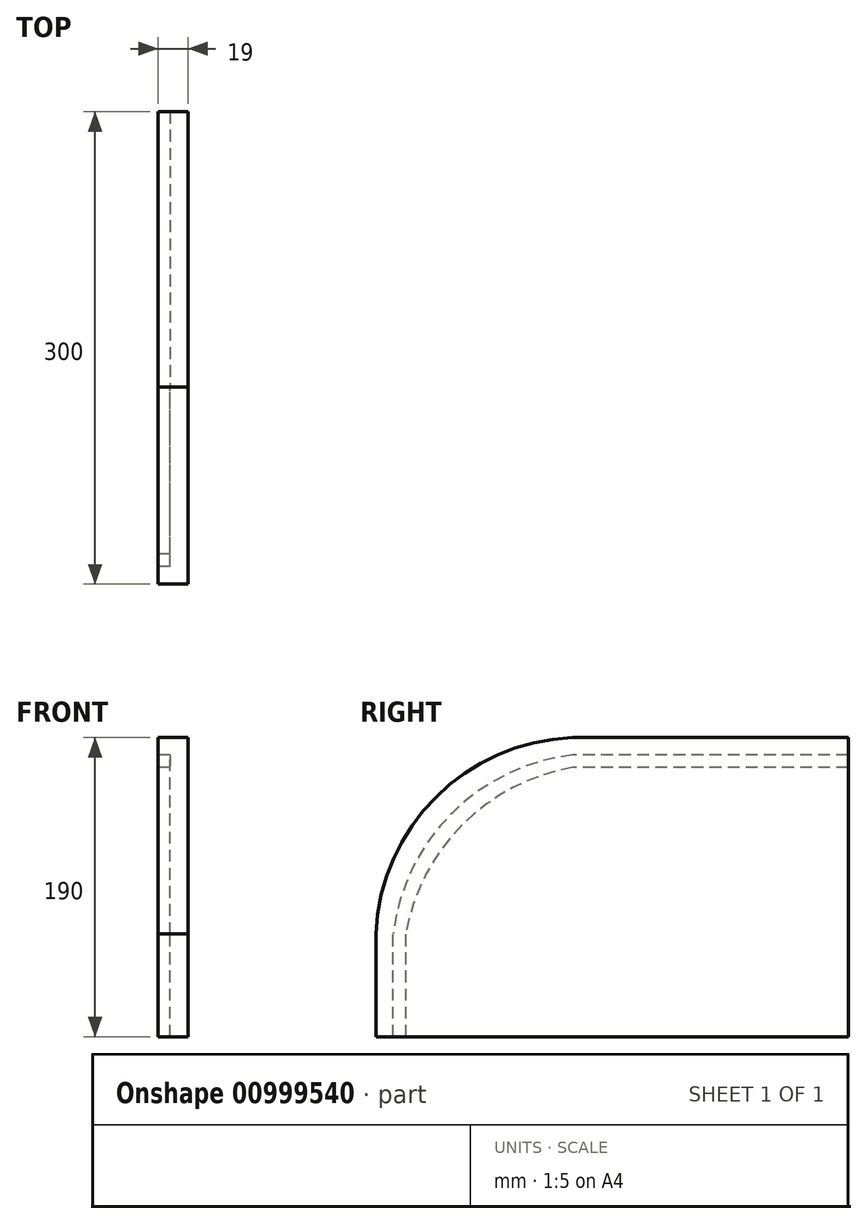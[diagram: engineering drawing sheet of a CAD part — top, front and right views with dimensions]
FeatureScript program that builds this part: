
annotation { "Feature Type Name" : "Feature", "Feature Type Description" : "" }
export const myFeature = defineFeature(function(context is Context, id is Id, definition is map)
    precondition{}
    {
        {
            var Q0;
            Q0=qCreatedBy(makeId("Right.planeOp"),FACE);
            var sketch = newSketch(context, id + "F0", { "sketchPlane" : qUnion([Q0]), "disableImprinting" : false});
            skLineSegment(sketch, "E0.bottom", {"start": v(-25, 95) * mm, "end": v(150, 95) * mm});
            skLineSegment(sketch, "E0.top", {"start": v(-150, -95) * mm, "end": v(150, -95) * mm});
            skLineSegment(sketch, "E0.left", {"start": v(-150, -29.82) * mm, "end": v(-150, -95) * mm});
            skLineSegment(sketch, "E0.right", {"start": v(150, 95) * mm, "end": v(150, -95) * mm});
            skPoint(sketch, "E0.middle", {"position": v(0, 0) * mm});
            skPoint(sketch, "E1", {"position": v(-150, -40) * mm});
            skPoint(sketch, "E2", {"position": v(-25, 95) * mm});
            skArc(sketch, "E3", {"start": v(-25, 95) * mm, "mid": v(-115.49, 53.42) * mm, "end": v(-150, -40) * mm});
            skPoint(sketch, "E4.orphan", {"position": v(-150, 95) * mm});
            skSolve(sketch);
        }
        {
            var Q0;
            {var subQ5=sQuery(id+"F0.wireOp",EDGE,"E0.bottom");Q0=makeQuery(id+"F0.imprint","IMPRINT",FACE,{"disambiguationData":[TD([[makeQuery(id+"F0.imprint","IMPRINT",EDGE,{"derivedFrom":subQ5}),-1.0]])]});}
            extrude(context, id + "F1", {"entities" : qUnion([Q0]), "flatOperationType" : FlatOperationType.REMOVE, "thickness1" : 5 * mm, "thickness2" : 0 * mm, "thickness" : 5 * mm, "depth" : 19 * mm, "offsetDistance" : 25 * mm, "startOffsetBound" : StartOffsetType.BLIND, "startOffsetDistance" : 25 * mm, "domain" : OperationDomain.MODEL});
        }
        {
            var Q0;
            Q0=makeQuery(id+"F1.opExtrude","CAP_FACE",FACE,{"disambiguationData":[OSD([sQuery(id+"F0.wireOp",EDGE,"E0.bottom"),sQuery(id+"F0.wireOp",EDGE,"E0.top"),sQuery(id+"F0.wireOp",EDGE,"E0.left"),sQuery(id+"F0.wireOp",EDGE,"E0.right"),sQuery(id+"F0.wireOp",EDGE,"E3")])],"isStart":true});
            var sketch = newSketch(context, id + "F2", { "sketchPlane" : qUnion([Q0]), "disableImprinting" : false});
            skPoint(sketch, "E5", {"position": v(-150, 84) * mm});
            skLineSegment(sketch, "E6", {"start": v(-150, 84) * mm, "end": v(25, 84) * mm});
            skPoint(sketch, "E7", {"position": v(-150, 76) * mm});
            skLineSegment(sketch, "E8", {"start": v(-150, 76) * mm, "end": v(25, 76) * mm});
            skPoint(sketch, "E9", {"position": v(139, -95) * mm});
            skPoint(sketch, "E10", {"position": v(131, -95) * mm});
            skLineSegment(sketch, "E11", {"start": v(139, -95) * mm, "end": v(139, -29.82) * mm});
            skLineSegment(sketch, "E12", {"start": v(131, -95) * mm, "end": v(131, -29.82) * mm});
            skArc(sketch, "E13", {"start": v(139, -29.82) * mm, "mid": v(101.75, 46.88) * mm, "end": v(25, 84) * mm});
            skArc(sketch, "E14", {"start": v(131, -29.82) * mm, "mid": v(94.77, 39.9) * mm, "end": v(25, 76) * mm});
            skSolve(sketch);
        }
        {
            var Q0;
            {var subQ1=sQuery(id+"F2.wireOp",EDGE,"E6");Q0=makeQuery(id+"F2.imprint","IMPRINT",FACE,{"disambiguationData":[TD([[makeQuery(id+"F2.imprint","IMPRINT",EDGE,{"derivedFrom":subQ1}),-1.0]])]});}
            extrude(context, id + "F3", {"entities" : qUnion([Q0]), "operationType" : NewBodyOperationType.REMOVE, "flatOperationType" : FlatOperationType.REMOVE, "thickness1" : 5 * mm, "thickness2" : 0 * mm, "thickness" : 5 * mm, "oppositeDirection" : true, "depth" : 7.5 * mm, "offsetDistance" : 25 * mm, "startOffsetBound" : StartOffsetType.BLIND, "startOffsetDistance" : 25 * mm, "domain" : OperationDomain.MODEL});
        }
    });
